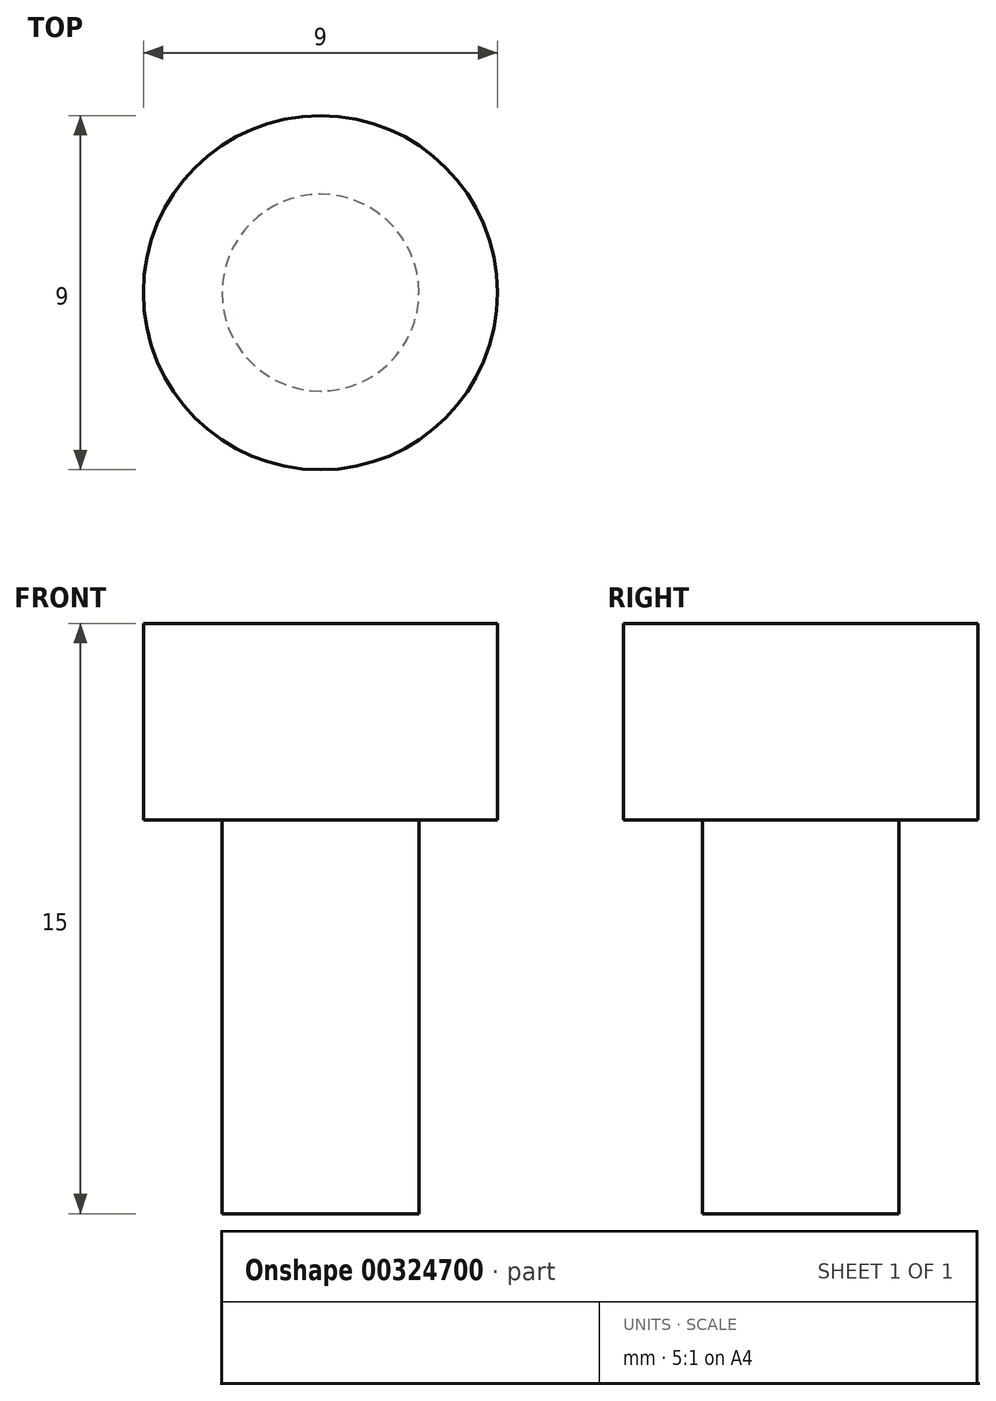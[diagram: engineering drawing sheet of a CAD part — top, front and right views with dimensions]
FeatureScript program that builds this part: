
annotation { "Feature Type Name" : "Feature", "Feature Type Description" : "" }
export const myFeature = defineFeature(function(context is Context, id is Id, definition is map)
    precondition{}
    {
        {
            var Q0;
            Q0=qCreatedBy(makeId("Top.planeOp"),FACE);
            var sketch = newSketch(context, id + "F0", { "sketchPlane" : qUnion([Q0])});
            skCircle(sketch, "E0", {"center": v(0, 0) * mm, "radius": 4.5 * mm});
            skSolve(sketch);
        }
        {
            var Q0;
            Q0=qSketchRegion(id+"F0",true);
            extrude(context, id + "F1", {"entities" : qUnion([Q0]), "depth" : 5 * mm});
        }
        {
            var Q0;
            Q0=makeQuery(id+"F1.opExtrude","CAP_FACE",FACE,{"disambiguationData":[OSD([sQuery(id+"F0.wireOp",EDGE,"E0")])],"isStart":true});
            var sketch = newSketch(context, id + "F2", { "sketchPlane" : qUnion([Q0])});
            skCircle(sketch, "E1", {"center": v(0, 0) * mm, "radius": 2.5 * mm});
            skSolve(sketch);
        }
        {
            var Q0;
            Q0=qSketchRegion(id+"F2",true);
            extrude(context, id + "F3", {"entities" : qUnion([Q0]), "operationType" : NewBodyOperationType.ADD, "depth" : 10 * mm});
        }
    });
